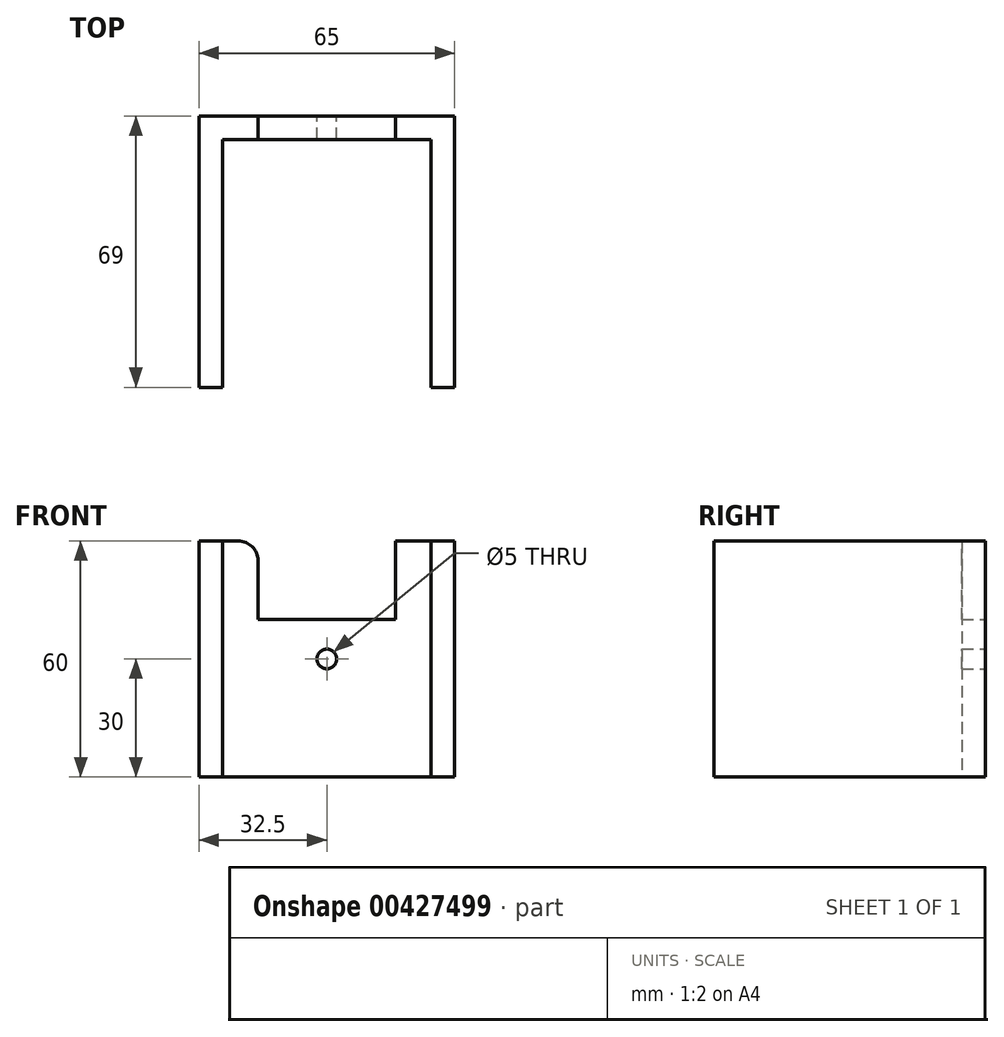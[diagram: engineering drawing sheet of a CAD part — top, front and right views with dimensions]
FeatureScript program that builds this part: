
annotation { "Feature Type Name" : "Feature", "Feature Type Description" : "" }
export const myFeature = defineFeature(function(context is Context, id is Id, definition is map)
    precondition{}
    {
        {
            var Q0;
            Q0=qCreatedBy(makeId("Top.planeOp"),FACE);
            var sketch = newSketch(context, id + "F0", { "sketchPlane" : qUnion([Q0])});
            skLineSegment(sketch, "E0", {"start": v(0, 0) * mm, "end": v(0, 69) * mm});
            skLineSegment(sketch, "E1", {"start": v(0, 69) * mm, "end": v(65, 69) * mm});
            skLineSegment(sketch, "E2", {"start": v(65, 69) * mm, "end": v(65, 0) * mm});
            skLineSegment(sketch, "E3", {"start": v(65, 0) * mm, "end": v(59, 0) * mm});
            skLineSegment(sketch, "E4", {"start": v(59, 0) * mm, "end": v(59, 63) * mm});
            skLineSegment(sketch, "E5", {"start": v(59, 63) * mm, "end": v(6, 63) * mm});
            skLineSegment(sketch, "E6", {"start": v(6, 63) * mm, "end": v(6, 0) * mm});
            skLineSegment(sketch, "E7", {"start": v(6, 0) * mm, "end": v(0, 0) * mm});
            skSolve(sketch);
        }
        {
            var Q0;
            Q0=makeQuery(id+"F0.imprint","IMPRINT",FACE,{"disambiguationData":[TD([[makeQuery(id+"F0.imprint","IMPRINT",EDGE,{"derivedFrom":sQuery(id+"F0.wireOp",EDGE,"E0")}),-1.0]])]});
            extrude(context, id + "F1", {"entities" : qUnion([Q0]), "depth" : 60 * mm});
        }
        {
            var Q0;
            Q0=makeQuery(id+"F1.opExtrude","SWEPT_FACE",FACE,{"disambiguationData":[OSD([sQuery(id+"F0.wireOp",EDGE,"E1")])]});
            var sketch = newSketch(context, id + "F2", { "sketchPlane" : qUnion([Q0])});
            skLineSegment(sketch, "E8.bottom", {"start": v(-65, 60) * mm, "end": v(0, 60) * mm});
            skLineSegment(sketch, "E8.top", {"start": v(-65, 0) * mm, "end": v(0, 0) * mm});
            skLineSegment(sketch, "E8.left", {"start": v(-65, 60) * mm, "end": v(-65, 0) * mm});
            skLineSegment(sketch, "E8.right", {"start": v(0, 60) * mm, "end": v(0, 0) * mm});
            skCircle(sketch, "E9", {"center": v(-32.5, 30) * mm, "radius": 11.98 * mm});
            skPoint(sketch, "E9.centerSnap0", {"position": v(-32.5, 0) * mm});
            skPoint(sketch, "E9.centerSnap1", {"position": v(0, 30) * mm});
            skSolve(sketch);
        }
        {
            var Q0;
            Q0=sQuery(id+"F2.wireOp",VERTEX,"E9.center");
            var Q1;
            Q1=makeQuery(id+"F1.opExtrude","SWEPT_BODY",BODY,{"disambiguationData":[OSD([sQuery(id+"F0.wireOp",EDGE,"E0"),sQuery(id+"F0.wireOp",EDGE,"E1"),sQuery(id+"F0.wireOp",EDGE,"E2"),sQuery(id+"F0.wireOp",EDGE,"E3"),sQuery(id+"F0.wireOp",EDGE,"E4"),sQuery(id+"F0.wireOp",EDGE,"E5"),sQuery(id+"F0.wireOp",EDGE,"E6"),sQuery(id+"F0.wireOp",EDGE,"E7")])]});
            hole(context, id + "F3", {"style" : HoleStyle.SIMPLE, "endStyle" : HoleEndStyle.THROUGH, "holeDiameter" : 5 * mm, "isTappedThrough" : true, "tappedDepth" : 12 * mm, "tapClearance" : 3, "locations" : qUnion([Q0]), "scope" : qUnion([Q1])});
        }
        {
            var Q0;
            Q0=makeQuery(id+"F1.opExtrude","SWEPT_FACE",FACE,{"disambiguationData":[OSD([sQuery(id+"F0.wireOp",EDGE,"E1")])]});
            var sketch = newSketch(context, id + "F4", { "sketchPlane" : qUnion([Q0])});
            skLineSegment(sketch, "E10", {"start": v(-32.5, 60) * mm, "end": v(-32.5, 30) * mm, "construction": true});
            skLineSegment(sketch, "E11", {"start": v(-15, 60) * mm, "end": v(-15, 40) * mm});
            skLineSegment(sketch, "E12", {"start": v(-15, 40) * mm, "end": v(-50, 40) * mm});
            skLineSegment(sketch, "E13", {"start": v(-50, 40) * mm, "end": v(-50, 60) * mm});
            skLineSegment(sketch, "E14", {"start": v(0, 30) * mm, "end": v(-65, 30) * mm, "construction": true});
            skSolve(sketch);
        }
        {
            var Q0;
            {var subQ0=sQuery(id+"F4.wireOp",EDGE,"E11");Q0=makeQuery(id+"F4.imprint","IMPRINT",FACE,{"disambiguationData":[TD([[makeQuery(id+"F4.imprint","IMPRINT",EDGE,{"derivedFrom":subQ0}),-1.0]])]});}
            extrude(context, id + "F5", {"entities" : qUnion([Q0]), "operationType" : NewBodyOperationType.REMOVE, "oppositeDirection" : true, "depth" : 25 * mm});
        }
        {
            var Q0;
            Q0=makeQuery(id+"F5.boolean.opBoolean","COPY",EDGE,{"derivedFrom":makeQuery(id+"F5.opExtrude","SWEPT_EDGE",EDGE,{"disambiguationData":[OSD([sQuery(id+"F0.wireOp",EDGE,"E1"),sQuery(id+"F4.wireOp",EDGE,"E11")])]})});
            var Q1;
            Q1=makeQuery(id+"F5.boolean.opBoolean","COPY",EDGE,{"derivedFrom":makeQuery(id+"F5.opExtrude","SWEPT_EDGE",EDGE,{"disambiguationData":[OSD([sQuery(id+"F0.wireOp",EDGE,"E1"),sQuery(id+"F4.wireOp",EDGE,"E13")])]})});
            fillet(context, id + "F6", {"entities" : qUnion([Q0, Q1]), "radius" : 5 * mm, "tangentPropagation" : true, "allowEdgeOverflow" : false});
        }
    });
